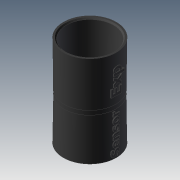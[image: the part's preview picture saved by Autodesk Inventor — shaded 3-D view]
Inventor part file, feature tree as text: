
AUTODESK INVENTOR PART (.ipt)
format: ipt  version: 2020 (Build 240168000, 168)  size: 491,520 bytes
history: native  units: mm
features: sketch x3, revolve x2, plane x1, extrude x1, chamfer x1
ambient origin geometry x8: Origin, YZ Plane, XZ Plane, XY Plane, X Axis, Y Axis, Z Axis, Center Point
bodies: Solid1 (feature_tree)
feature tree (8):
  revolve  "Revolution1"  [1 undecoded]
  revolve  "Revolution2"  [1 undecoded]
  plane  "Work Plane1"
  extrude  "Extrusion1"  TaperAngle=0.0deg  [1 undecoded]
  chamfer  "Chamfer1"  [1 undecoded]
  sketch  "Sketch1"  dims[d0=11.25mm d1=20.0mm]
  sketch  "Sketch2"  dims[d2=11.0mm d3=6.5mm]
  sketch  "Sketch3"  dims[d4=1.35mm d5=0.0mm d6=0.0mm d7=90.0deg d8=11.25mm d9=25.0mm d10=11.0mm d11=3.5mm d13=2.0mm d14=15.80796mm d15=1.35mm d16=90.0deg d17=12.75mm d18=10.0mm d19=0.0mm d20=0.6mm d21=2.0mm d22=45.0deg]
note: 4 required parameter values undecoded (feature->parameter linkage not recoverable at this tier; creation-order binding heuristic only, values carry confidence <= 0.55)